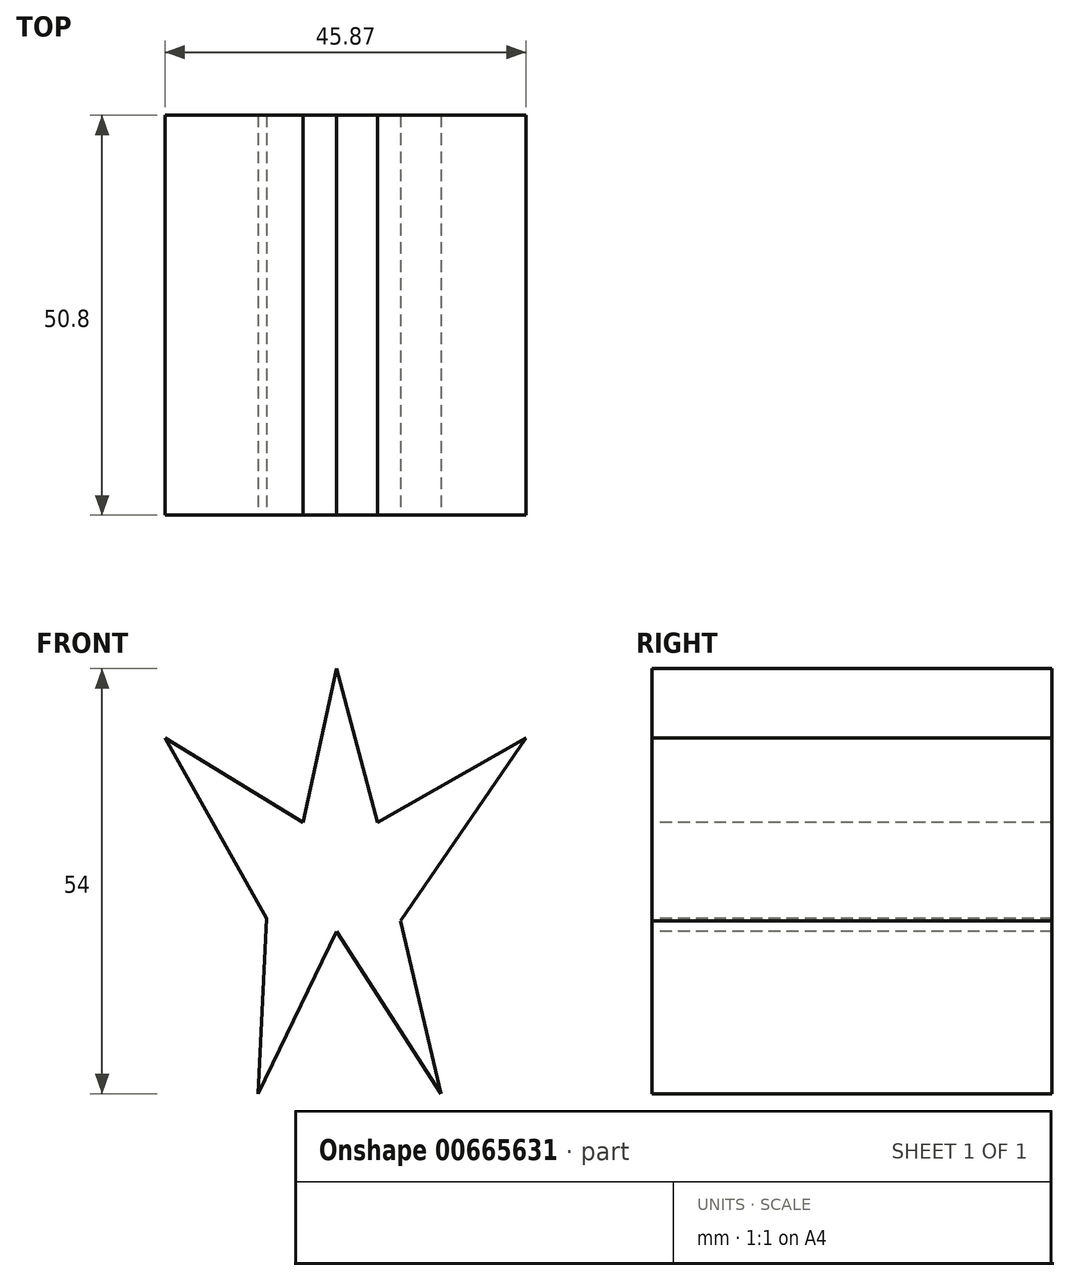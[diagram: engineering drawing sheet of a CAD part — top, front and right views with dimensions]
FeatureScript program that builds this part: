
annotation { "Feature Type Name" : "Feature", "Feature Type Description" : "" }
export const myFeature = defineFeature(function(context is Context, id is Id, definition is map)
    precondition{}
    {
        {
            var Q0;
            Q0=qCreatedBy(makeId("Front.planeOp"),FACE);
            var sketch = newSketch(context, id + "F0", { "sketchPlane" : qUnion([Q0])});
            skLineSegment(sketch, "E0", {"start": v(0, 0) * mm, "end": v(13.27, -20.63) * mm});
            skLineSegment(sketch, "E1", {"start": v(0, 0) * mm, "end": v(-9.98, -20.63) * mm});
            skLineSegment(sketch, "E2", {"start": v(-9.98, -20.63) * mm, "end": v(-8.86, 1.62) * mm});
            skLineSegment(sketch, "E3", {"start": v(-8.86, 1.62) * mm, "end": v(-21.78, 24.58) * mm});
            skLineSegment(sketch, "E4", {"start": v(13.27, -20.63) * mm, "end": v(8.12, 1.33) * mm});
            skLineSegment(sketch, "E5", {"start": v(-21.78, 24.58) * mm, "end": v(-4.26, 13.85) * mm});
            skLineSegment(sketch, "E6", {"start": v(8.12, 1.33) * mm, "end": v(24.1, 24.58) * mm});
            skLineSegment(sketch, "E7", {"start": v(24.1, 24.58) * mm, "end": v(5.24, 13.85) * mm});
            skLineSegment(sketch, "E8", {"start": v(-4.26, 13.85) * mm, "end": v(0, 33.37) * mm});
            skLineSegment(sketch, "E9", {"start": v(0, 33.37) * mm, "end": v(5.24, 13.85) * mm});
            skSolve(sketch);
        }
        {
            var Q0;
            Q0=makeQuery(id+"F0.imprint","IMPRINT",FACE,{"disambiguationData":[TD([[makeQuery(id+"F0.imprint","IMPRINT",EDGE,{"derivedFrom":sQuery(id+"F0.wireOp",EDGE,"E0")}),1.0]])]});
            extrude(context, id + "F1", {"entities" : qUnion([Q0]), "oppositeDirection" : true, "depth" : 50.8 * mm, "offsetDistance" : 25.4 * mm});
        }
    });
